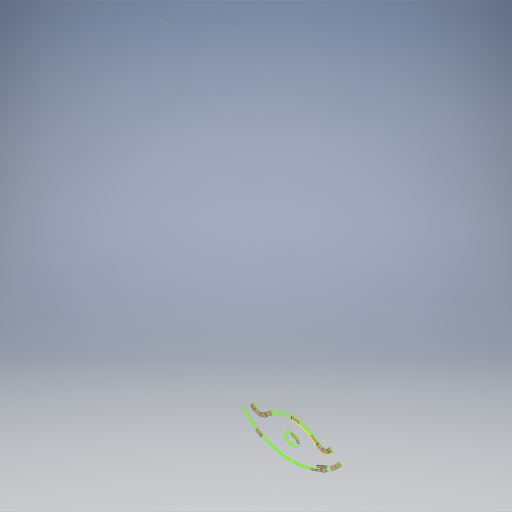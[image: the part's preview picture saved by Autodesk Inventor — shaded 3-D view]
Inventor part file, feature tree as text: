
AUTODESK INVENTOR PART (.ipt)
format: ipt  version: 2023 (Build 270158030, 158C)  size: 1,111,552 bytes
history: native  units: in
note: dims shown in document units (in); Inventor stores cm internally (conversion verified against a paired STEP export)
features: sketch x13, extrude x12, other x5, projected_geometry x4, plane x3, sweep x3, mirror x2
ambient origin geometry x8: Origin, YZ Plane, XZ Plane, XY Plane, X Axis, Y Axis, Z Axis, Center Point
bodies: Solid9 (feature_tree), Solid10 (feature_tree), Solid11 (feature_tree), Solid12 (feature_tree), Solid15 (feature_tree), Solid16 (feature_tree), Solid17 (feature_tree), Solid18 (feature_tree), Solid19 (feature_tree), Solid20 (feature_tree), Solid21 (feature_tree), Solid22 (feature_tree), Solid27 (feature_tree), Solid28 (feature_tree), Solid29 (feature_tree), Solid30 (feature_tree), Solid31 (feature_tree)
feature tree (42):
  sketch  "Sketch1"  dims[d14=6.125in d15=0.0in d16=6.125in d17=0.0in]
  plane  "Work Plane1"
  sketch  "Sketch2"  dims[d18=6.125in d19=0.0in d20=6.125in d21=0.0in]
  extrude  "A 2"  Depth=6.125in TaperAngle=0.0deg
  extrude  "B 4"  Depth=6.125in TaperAngle=0.0deg
  extrude  "D 2"  [1 undecoded]
  extrude  "E 10"  Depth=6.125in TaperAngle=0.0deg
  extrude  "F 2"  Depth=6.125in TaperAngle=0.0deg
  extrude  "G 10"  Depth=6.125in TaperAngle=0.0deg
  extrude  "I 4"  Depth=6.125in TaperAngle=0.0deg
  extrude  "J 1"  Depth=0.25in
  extrude  "K 1"  TaperAngle=0.0deg  [1 undecoded]
  extrude  "N 6"  Depth=0.125in
  sketch  "Sketch3"  dims[d22=6.125in d23=0.0in d28=-36.0in]
  sweep  "Sweep2"
  sweep  "Sweep3"
  extrude  "Extrusion27"  Depth=0.375in
  plane  "Work Plane2"
  extrude  "Extrusion28"  Depth=0.25in
  sketch  "Sketch12"  dims[d63=0.125in d64=0.125in]
  sketch  "Sketch13"  dims[d65=0.125in d66=0.25in d67=0.25in d68=0.375in d69=0.25in d70=0.25in d71=0.375in d72=0.0in d73=0.0in d74=6.0in d75=0.0in d76=0.125in d77=90.0deg d78=6.0in d79=24.375in d80=0.0in d81=1.5005in d82=0.0in d83=20.0in d84=0.125in d85=0.125in d86=0.2125in d87=0.0in d88=0.0in d89=0.25in d90=0.25in d91=0.375in]
  sweep  "Sweep4"
  mirror  "Mirror1"
  mirror  "Mirror2"
  sketch  "Sketch4"  dims[d29=6.125in d30=0.0in d31=6.125in d32=0.0in]
  sketch  "Sketch6"  dims[d33=6.0in d34=0.0in d35=6.125in d36=0.0in]
  projected_geometry  "Projected Loop2"
  sketch  "Sketch7"  dims[d37=6.125in d38=0.0in d39=6.125in d40=0.0in]
  projected_geometry  "Projected Loop3"
  sketch  "Sketch8"  dims[d41=6.125in d42=0.0in d43=6.125in d44=0.0in]
  sketch  "3D Sketch1"
  sketch  "Sketch10"  dims[d57=0.25in d58=0.25in]
  projected_geometry  "Projected Loop4"
  projected_geometry  "Projected Loop5"
  sketch  "Sketch11"  dims[d59=0.375in d60=0.0in d61=0.0in]
  sketch  "3D Sketch2"
  other  "Pattern of Solid18:1"
  other  "Pattern of Solid19:2"
  other  "Pattern of Solid20:3"
  other  "Pattern of Solid21:4"
  other  "Pattern of Solid10:5"
  plane  "Work Plane3"
note: 2 required parameter values undecoded (feature->parameter linkage not recoverable at this tier; creation-order binding heuristic only, values carry confidence <= 0.55)
